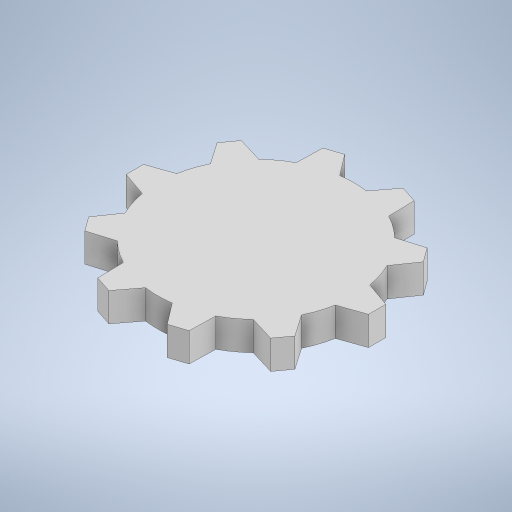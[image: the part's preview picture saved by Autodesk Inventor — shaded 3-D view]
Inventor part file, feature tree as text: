
AUTODESK INVENTOR PART (.ipt)
format: ipt  version: 2023 (Build 270158000, 158)  size: 294,400 bytes
history: native  units: in
note: dims shown in document units (in); Inventor stores cm internally (conversion verified against a paired STEP export)
features: extrude x1, sketch x1
ambient origin geometry x8: Origin, YZ Plane, XZ Plane, XY Plane, X Axis, Y Axis, Z Axis, Center Point
bodies: Solid1 (feature_tree)
feature tree (2):
  extrude  "Extrusion1"  Depth=0.1969in
  sketch  "Sketch1"  dims[d0=1.3386in d1=0.1181in d2=0.2362in d3=0.1575in d4=0.7515in d5=0.7515in d6=3.937in d8=360.0deg d10=0.1969in d11=0.0in]
